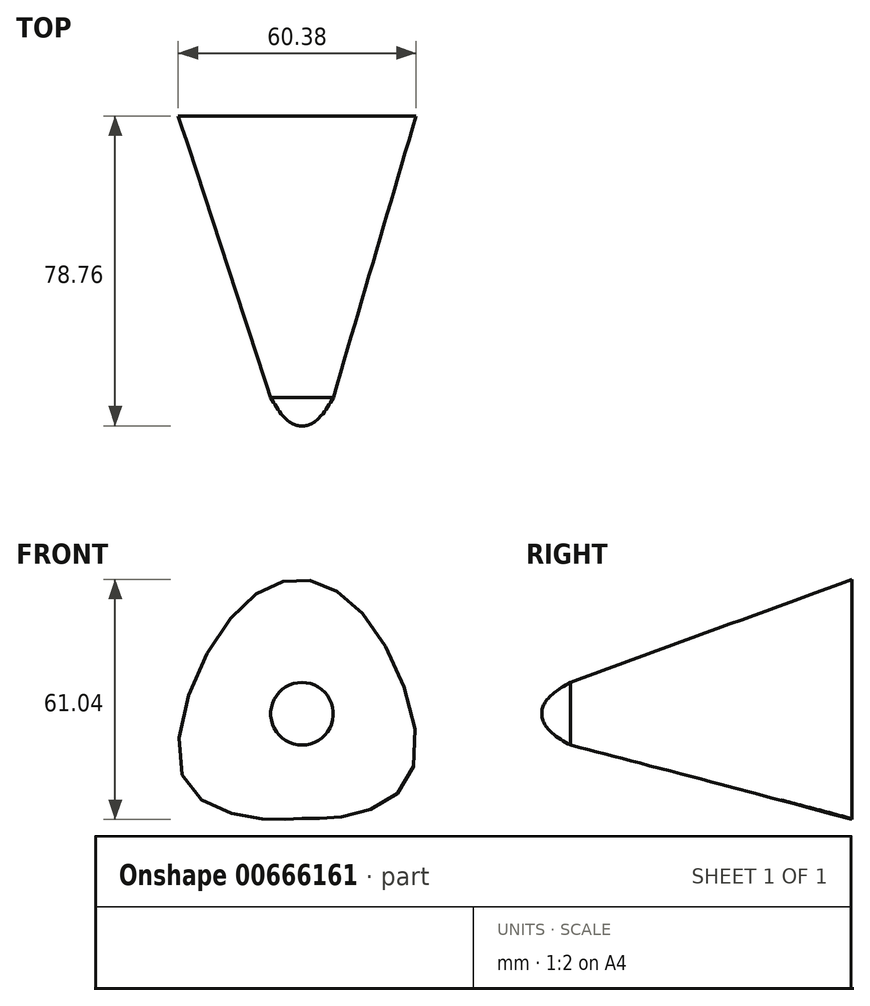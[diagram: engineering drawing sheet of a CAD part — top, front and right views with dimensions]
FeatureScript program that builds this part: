
annotation { "Feature Type Name" : "Feature", "Feature Type Description" : "" }
export const myFeature = defineFeature(function(context is Context, id is Id, definition is map)
    precondition{}
    {
        {
            var Q0;
            Q0=qCreatedBy(makeId("Top.planeOp"),FACE);
            var sketch = newSketch(context, id + "F0", { "sketchPlane" : qUnion([Q0])});
            skLineSegment(sketch, "E0", {"start": v(253.45, -2.2) * mm, "end": v(144.23, -2.2) * mm, "construction": true});
            skLineSegment(sketch, "E1", {"start": v(-24.76, -111.5) * mm, "end": v(-94.47, -47.22) * mm});
            skLineSegment(sketch, "E2", {"start": v(-94.47, -47.22) * mm, "end": v(-121.4, -22.6) * mm});
            skLineSegment(sketch, "E3", {"start": v(-121.4, -22.6) * mm, "end": v(-159.94, 12.6) * mm});
            skLineSegment(sketch, "E4", {"start": v(-159.94, 12.6) * mm, "end": v(-239.83, 79.14) * mm});
            skLineSegment(sketch, "E5", {"start": v(-239.83, 79.14) * mm, "end": v(-239.83, 92.25) * mm});
            skLineSegment(sketch, "E6", {"start": v(-239.83, 92.25) * mm, "end": v(-238.6, 109.82) * mm});
            skLineSegment(sketch, "E7", {"start": v(-238.6, 109.82) * mm, "end": v(-214.43, 91.8) * mm});
            skLineSegment(sketch, "E8", {"start": v(-214.43, 91.8) * mm, "end": v(-157.8, 58.63) * mm});
            skLineSegment(sketch, "E9", {"start": v(-157.8, 58.63) * mm, "end": v(-98.23, 23.74) * mm});
            skLineSegment(sketch, "E10", {"start": v(-98.23, 23.74) * mm, "end": v(-85.21, 19.66) * mm});
            skLineSegment(sketch, "E11", {"start": v(-85.21, 19.66) * mm, "end": v(-49.36, 8.07) * mm});
            skLineSegment(sketch, "E12", {"start": v(-49.36, 8.07) * mm, "end": v(-24.76, 0.11) * mm});
            skLineSegment(sketch, "E13", {"start": v(-24.76, 0.11) * mm, "end": v(-24.76, -111.5) * mm});
            skLineSegment(sketch, "E14", {"start": v(0.24, -271.03) * mm, "end": v(0.24, 270.74) * mm});
            skLineSegment(sketch, "E15.MirrorCS", {"start": v(25.24, 0.11) * mm, "end": v(25.24, -111.5) * mm});
            skLineSegment(sketch, "E16.MirrorCS", {"start": v(25.24, -111.5) * mm, "end": v(94.96, -47.22) * mm});
            skLineSegment(sketch, "E17.MirrorCS", {"start": v(94.96, -47.22) * mm, "end": v(121.9, -22.6) * mm});
            skLineSegment(sketch, "E18.MirrorCS", {"start": v(121.9, -22.6) * mm, "end": v(160.43, 12.6) * mm});
            skLineSegment(sketch, "E19.MirrorCS", {"start": v(160.43, 12.6) * mm, "end": v(240.32, 79.14) * mm});
            skLineSegment(sketch, "E20.MirrorCS", {"start": v(85.7, 19.66) * mm, "end": v(49.85, 8.07) * mm});
            skLineSegment(sketch, "E21.MirrorCS", {"start": v(98.72, 23.74) * mm, "end": v(85.7, 19.66) * mm});
            skLineSegment(sketch, "E22.MirrorCS", {"start": v(49.85, 8.07) * mm, "end": v(25.24, 0.11) * mm});
            skLineSegment(sketch, "E23.MirrorCS", {"start": v(158.29, 58.63) * mm, "end": v(98.72, 23.74) * mm});
            skLineSegment(sketch, "E24.MirrorCS", {"start": v(214.92, 91.8) * mm, "end": v(158.29, 58.63) * mm});
            skLineSegment(sketch, "E25.MirrorCS", {"start": v(239.08, 109.82) * mm, "end": v(214.92, 91.8) * mm});
            skLineSegment(sketch, "E26.MirrorCS", {"start": v(240.32, 92.25) * mm, "end": v(239.08, 109.82) * mm});
            skLineSegment(sketch, "E27.MirrorCS", {"start": v(240.32, 79.14) * mm, "end": v(240.32, 92.25) * mm});
            skLineSegment(sketch, "E28", {"start": v(-5.03, 241.98) * mm, "end": v(-29.26, 248.65) * mm});
            skLineSegment(sketch, "E29", {"start": v(-29.26, 248.65) * mm, "end": v(-84.68, 263.65) * mm});
            skLineSegment(sketch, "E30", {"start": v(-84.68, 263.65) * mm, "end": v(-84.68, 244.37) * mm});
            skLineSegment(sketch, "E31", {"start": v(-84.68, 244.37) * mm, "end": v(-19.34, 185.62) * mm});
            skPoint(sketch, "E32", {"position": v(-17.44, 180) * mm});
            skArc(sketch, "E33", {"start": v(-17.44, 180) * mm, "mid": v(-17.66, 183.06) * mm, "end": v(-19.34, 185.62) * mm});
            skLineSegment(sketch, "E34", {"start": v(-24.76, 0.11) * mm, "end": v(-24.76, 94.24) * mm});
            skArc(sketch, "E35", {"start": v(-17.44, 180) * mm, "mid": v(-22.92, 137.28) * mm, "end": v(-24.76, 94.24) * mm});
            skLineSegment(sketch, "E36.MirrorCS", {"start": v(25.24, 0.11) * mm, "end": v(25.24, 94.24) * mm});
            skArc(sketch, "E37.MirrorCS", {"start": v(17.93, 180) * mm, "mid": v(23.41, 137.28) * mm, "end": v(25.24, 94.24) * mm});
            skArc(sketch, "E38.MirrorCS", {"start": v(17.93, 180) * mm, "mid": v(18.15, 183.06) * mm, "end": v(19.83, 185.62) * mm});
            skLineSegment(sketch, "E39.MirrorCS", {"start": v(85.17, 244.37) * mm, "end": v(19.83, 185.62) * mm});
            skLineSegment(sketch, "E40.MirrorCS", {"start": v(85.17, 263.65) * mm, "end": v(85.17, 244.37) * mm});
            skLineSegment(sketch, "E41.MirrorCS", {"start": v(29.75, 248.65) * mm, "end": v(85.17, 263.65) * mm});
            skLineSegment(sketch, "E42.MirrorCS", {"start": v(5.52, 241.98) * mm, "end": v(29.75, 248.65) * mm});
            skLineSegment(sketch, "E43", {"start": v(-24.76, -111.5) * mm, "end": v(-24.76, -164.18) * mm});
            skFitSpline(sketch, "E44", {"points": [v(-24.76, -164.18) * mm, v(0.24, -271.03) * mm], "startDerivative": vector(-1.52, -118.16) * mm, "endDerivative": vector(37.88, 3.46) * mm});
            skFitSpline(sketch, "E45.MirrorCS", {"points": [v(25.24, -164.18) * mm, v(0.24, -271.03) * mm], "startDerivative": vector(1.52, -118.16) * mm, "endDerivative": vector(-37.88, 3.46) * mm});
            skLineSegment(sketch, "E46.MirrorCS", {"start": v(25.24, -111.5) * mm, "end": v(25.24, -164.18) * mm});
            skArc(sketch, "E47", {"start": v(-17.44, 180) * mm, "mid": v(-10.14, 210.77) * mm, "end": v(-5.03, 241.98) * mm});
            skPoint(sketch, "E48", {"position": v(0.24, 254.5) * mm});
            skArc(sketch, "E49", {"start": v(0.24, 254.5) * mm, "mid": v(-3, 248.5) * mm, "end": v(-5.03, 241.98) * mm});
            skArc(sketch, "E50.MirrorCS", {"start": v(17.93, 180) * mm, "mid": v(10.63, 210.77) * mm, "end": v(5.52, 241.98) * mm});
            skArc(sketch, "E51.MirrorCS", {"start": v(0.24, 254.5) * mm, "mid": v(3.48, 248.5) * mm, "end": v(5.52, 241.98) * mm});
            skLineSegment(sketch, "E52", {"start": v(25.24, -164.18) * mm, "end": v(-24.76, -164.18) * mm});
            skLineSegment(sketch, "E53", {"start": v(25.24, -111.5) * mm, "end": v(-24.76, -111.5) * mm});
            skLineSegment(sketch, "E54.trimOffspring", {"start": v(-143.74, -2.2) * mm, "end": v(-246.55, -2.2) * mm, "construction": true});
            skLineSegment(sketch, "E55", {"start": v(25.24, 0.11) * mm, "end": v(-24.76, 0.11) * mm});
            skLineSegment(sketch, "E56", {"start": v(25.24, 94.24) * mm, "end": v(-24.76, 94.24) * mm});
            skLineSegment(sketch, "E57", {"start": v(7.9, -263.86) * mm, "end": v(-7.4, -263.86) * mm, "construction": true});
            skSolve(sketch);
        }
        {
            var Q0;
            Q0=qCreatedBy(makeId("Front.planeOp"),FACE);
            var sketch = newSketch(context, id + "F1", { "sketchPlane" : qUnion([Q0])});
            skPoint(sketch, "E58.0", {"position": v(0.24, 0) * mm});
            skPoint(sketch, "E59.0", {"position": v(253.45, 0) * mm});
            skFitSpline(sketch, "E60", {"points": [v(0, -21.3) * mm, v(20.68, -8.28) * mm, v(15.56, 24.4) * mm, v(-0.7, 35.47) * mm, v(-17.24, 24.52) * mm, v(-22.43, -8.74) * mm, v(0, -21.3) * mm]});
            skSolve(sketch);
        }
        {
            var Q0;
            Q0=qCreatedBy(makeId("Right.planeOp"),FACE);
            var sketch = newSketch(context, id + "F2", { "sketchPlane" : qUnion([Q0])});
            skPoint(sketch, "E61.0", {"position": v(274.75, 0) * mm});
            skPoint(sketch, "E62", {"position": v(-236.52, 28.3) * mm});
            skPoint(sketch, "E63", {"position": v(-101.02, 40) * mm});
            skPoint(sketch, "E64", {"position": v(-35.88, 32.77) * mm});
            skFitSpline(sketch, "E65", {"points": [v(-236.52, 28.3) * mm, v(-271.17, 9.16) * mm, v(-179.93, -18.65) * mm], "startDerivative": vector(-135, -52.75) * mm, "endDerivative": vector(226.64, -8.41) * mm});
            skLineSegment(sketch, "E66", {"start": v(-236.52, 28.3) * mm, "end": v(-236.52, -9.96) * mm});
            skLineSegment(sketch, "E67", {"start": v(-236.52, 9.16) * mm, "end": v(-271.17, 9.16) * mm});
            skFitSpline(sketch, "E68", {"points": [v(-35.88, 32.77) * mm, v(-67.84, 36.16) * mm, v(-101.02, 40) * mm, v(-192.42, 40) * mm, v(-222.23, 38.06) * mm, v(-232.62, 32.77) * mm, v(-236.52, 28.3) * mm], "startDerivative": vector(-204.87, 13.24) * mm, "endDerivative": vector(-43.24, -59.83) * mm});
            skLineSegment(sketch, "E69", {"start": v(-263.97, 1.04) * mm, "end": v(-263.97, 17.12) * mm});
            skSolve(sketch);
        }
        {
            var Q0;
            {var subQ0=sQuery(id+"F2.wireOp",EDGE,"E67");var subQ1=sQuery(id+"F2.wireOp",EDGE,"E65");var subQ2=makeQuery(id+"F2.imprint","INTERSECT",VERTEX,{"derivedFrom":[subQ1,subQ0]});Q0=makeQuery(id+"F2.imprint","IMPRINT",FACE,{"disambiguationData":[TD([[makeQuery(id+"F2.imprint","IMPRINT",EDGE,{"disambiguationData":[TD([[subQ2,1.0]])],"derivedFrom":subQ1}),1.0]])]});}
            var Q1;
            Q1=sQuery(id+"F2.wireOp",EDGE,"E67");
            revolve(context, id + "F3", {"entities" : qUnion([Q0]), "axis" : qUnion([Q1]), "revolveType" : RevolveType.FULL});
        }
        {
            var Q0;
            Q0=makeQuery(id+"F1.imprint","IMPRINT",FACE,{"disambiguationData":[TD([[makeQuery(id+"F1.imprint","IMPRINT",EDGE,{"derivedFrom":sQuery(id+"F1.wireOp",EDGE,"E60")}),1.0]])]});
            cPlane(context, id + "F4", {"entities" : qUnion([Q0]), "cplaneType" : CPlaneType.OFFSET, "offset" : 192.42 * mm, "width" : 150 * mm, "height" : 150 * mm});
        }
        {
            var Q0;
            Q0=qCreatedBy(id+"F4.planeOp",FACE);
            var sketch = newSketch(context, id + "F5", { "sketchPlane" : qUnion([Q0])});
            skFitSpline(sketch, "E70.0", {"points": [v(0.04, -17.43) * mm, v(8.95, -17.22) * mm, v(27.3, -7.11) * mm, v(18.83, 30.06) * mm, v(-0.64, 43.3) * mm, v(-20.47, 30.33) * mm, v(-29.66, -8.07) * mm, v(-9.1, -17.65) * mm, v(0.04, -17.43) * mm]});
            skPoint(sketch, "E71.0", {"position": v(0, 40) * mm});
            skSolve(sketch);
        }
        {
            var Q1;
            Q1=makeQuery(id+"F5.imprint","IMPRINT",FACE,{"disambiguationData":[TD([[makeQuery(id+"F5.imprint","IMPRINT",EDGE,{"derivedFrom":sQuery(id+"F5.wireOp",EDGE,"E70.0")}),1.0]])]});
            var Q2;
            Q2=makeQuery(id+"F3.opRevolve","SWEPT_FACE",FACE,{"disambiguationData":[OSD([sQuery(id+"F2.wireOp",EDGE,"E69")])]});
            loft(context, id + "F6", {"operationType" : NewBodyOperationType.ADD, "sheetProfilesArray" : [{ "sheetProfileEntities" : qUnion([Q1]) }, { "sheetProfileEntities" : qUnion([Q2]) }]});
        }
    });
